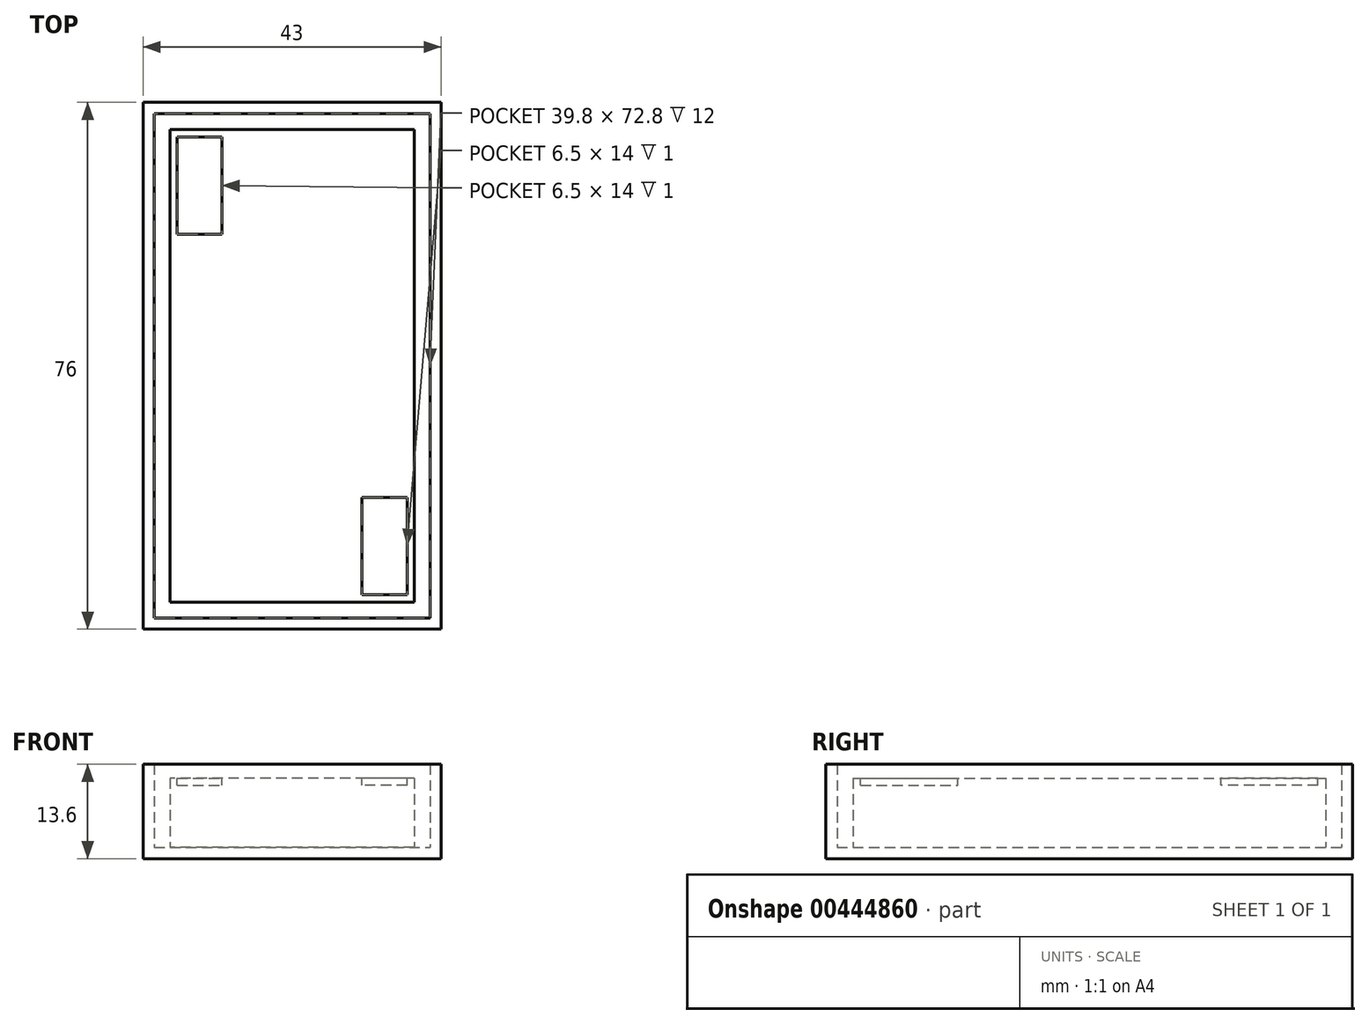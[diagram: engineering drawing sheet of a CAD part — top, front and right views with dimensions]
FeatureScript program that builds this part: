
annotation { "Feature Type Name" : "Feature", "Feature Type Description" : "" }
export const myFeature = defineFeature(function(context is Context, id is Id, definition is map)
    precondition{}
    {
        {
            var Q0;
            Q0=qCreatedBy(makeId("Top.planeOp"),FACE);
            var sketch = newSketch(context, id + "F0", { "sketchPlane" : qUnion([Q0])});
            skLineSegment(sketch, "E0.bottom", {"start": v(17.6, -34.1) * mm, "end": v(-17.6, -34.1) * mm});
            skLineSegment(sketch, "E0.top", {"start": v(17.6, 34.1) * mm, "end": v(-17.6, 34.1) * mm});
            skLineSegment(sketch, "E0.left", {"start": v(17.6, -34.1) * mm, "end": v(17.6, 34.1) * mm});
            skLineSegment(sketch, "E0.right", {"start": v(-17.6, -34.1) * mm, "end": v(-17.6, 34.1) * mm});
            skPoint(sketch, "E0.middle", {"position": v(0, 0) * mm});
            skSolve(sketch);
        }
        {
            var Q0;
            Q0 = qSketchRegion(id + "F0", true);
            extrude(context, id + "F1", {"entities" : qUnion([Q0]), "depth" : 10 * mm});
        }
        {
            var Q0;
            Q0=makeQuery(id+"F1.opExtrude","CAP_FACE",FACE,{"disambiguationData":[OSD([sQuery(id+"F0.wireOp",EDGE,"E0.bottom"),sQuery(id+"F0.wireOp",EDGE,"E0.top"),sQuery(id+"F0.wireOp",EDGE,"E0.left"),sQuery(id+"F0.wireOp",EDGE,"E0.right")])],"isStart":false});
            var sketch = newSketch(context, id + "F2", { "sketchPlane" : qUnion([Q0])});
            skLineSegment(sketch, "E1.bottom", {"start": v(-16.6, 33) * mm, "end": v(-10.1, 33) * mm});
            skLineSegment(sketch, "E1.top", {"start": v(-16.6, 19) * mm, "end": v(-10.1, 19) * mm});
            skLineSegment(sketch, "E1.left", {"start": v(-16.6, 33) * mm, "end": v(-16.6, 19) * mm});
            skLineSegment(sketch, "E1.right", {"start": v(-10.1, 33) * mm, "end": v(-10.1, 19) * mm});
            skPoint(sketch, "E1.middle", {"position": v(-13.35, 26) * mm});
            skLineSegment(sketch, "E2.bottom", {"start": v(16.6, -33) * mm, "end": v(10.1, -33) * mm});
            skLineSegment(sketch, "E2.top", {"start": v(16.6, -19) * mm, "end": v(10.1, -19) * mm});
            skLineSegment(sketch, "E2.left", {"start": v(16.6, -33) * mm, "end": v(16.6, -19) * mm});
            skLineSegment(sketch, "E2.right", {"start": v(10.1, -33) * mm, "end": v(10.1, -19) * mm});
            skPoint(sketch, "E2.middle", {"position": v(13.35, -26) * mm});
            skSolve(sketch);
        }
        {
            var Q0;
            Q0 = qSketchRegion(id + "F2", true);
            extrude(context, id + "F3", {"entities" : qUnion([Q0]), "operationType" : NewBodyOperationType.REMOVE, "oppositeDirection" : true, "depth" : 1 * mm});
        }
        {
            var Q0;
            Q0=makeQuery(id+"F1.opExtrude","CAP_FACE",FACE,{"disambiguationData":[OSD([sQuery(id+"F0.wireOp",EDGE,"E0.bottom"),sQuery(id+"F0.wireOp",EDGE,"E0.top"),sQuery(id+"F0.wireOp",EDGE,"E0.left"),sQuery(id+"F0.wireOp",EDGE,"E0.right")])],"isStart":true});
            var sketch = newSketch(context, id + "F4", { "sketchPlane" : qUnion([Q0])});
            skLineSegment(sketch, "E3.bottom", {"start": v(21.5, -38) * mm, "end": v(-21.5, -38) * mm});
            skLineSegment(sketch, "E3.top", {"start": v(21.5, 38) * mm, "end": v(-21.5, 38) * mm});
            skLineSegment(sketch, "E3.left", {"start": v(21.5, -38) * mm, "end": v(21.5, 38) * mm});
            skLineSegment(sketch, "E3.right", {"start": v(-21.5, -38) * mm, "end": v(-21.5, 38) * mm});
            skPoint(sketch, "E3.middle", {"position": v(0, 0) * mm});
            skSolve(sketch);
        }
        {
            var Q0;
            Q0 = qSketchRegion(id + "F4", true);
            extrude(context, id + "F5", {"entities" : qUnion([Q0]), "depth" : 1.6 * mm});
        }
        {
            var Q0;
            Q0=makeQuery(id+"F5.opExtrude","CAP_FACE",FACE,{"disambiguationData":[OSD([sQuery(id+"F4.wireOp",EDGE,"E3.bottom"),sQuery(id+"F4.wireOp",EDGE,"E3.top"),sQuery(id+"F4.wireOp",EDGE,"E3.left"),sQuery(id+"F4.wireOp",EDGE,"E3.right")])],"isStart":true});
            var sketch = newSketch(context, id + "F6", { "sketchPlane" : qUnion([Q0])});
            skLineSegment(sketch, "E4.0", {"start": v(19.9, -36.4) * mm, "end": v(19.9, 36.4) * mm});
            skLineSegment(sketch, "E4.1", {"start": v(-19.9, -36.4) * mm, "end": v(19.9, -36.4) * mm});
            skLineSegment(sketch, "E4.2", {"start": v(-19.9, 36.4) * mm, "end": v(-19.9, -36.4) * mm});
            skLineSegment(sketch, "E4.3", {"start": v(19.9, 36.4) * mm, "end": v(-19.9, 36.4) * mm});
            skSolve(sketch);
        }
        {
            var Q0;
            Q0=makeQuery(id+"F6.imprint","IMPRINT",FACE,{"disambiguationData":[TD([[makeQuery(id+"F6.imprint","IMPRINT",EDGE,{"derivedFrom":sQuery(id+"F6.wireOp",EDGE,"E4.0")}),-1.0]])]});
            extrude(context, id + "F7", {"entities" : qUnion([Q0]), "operationType" : NewBodyOperationType.ADD, "depth" : 12 * mm});
        }
    });
